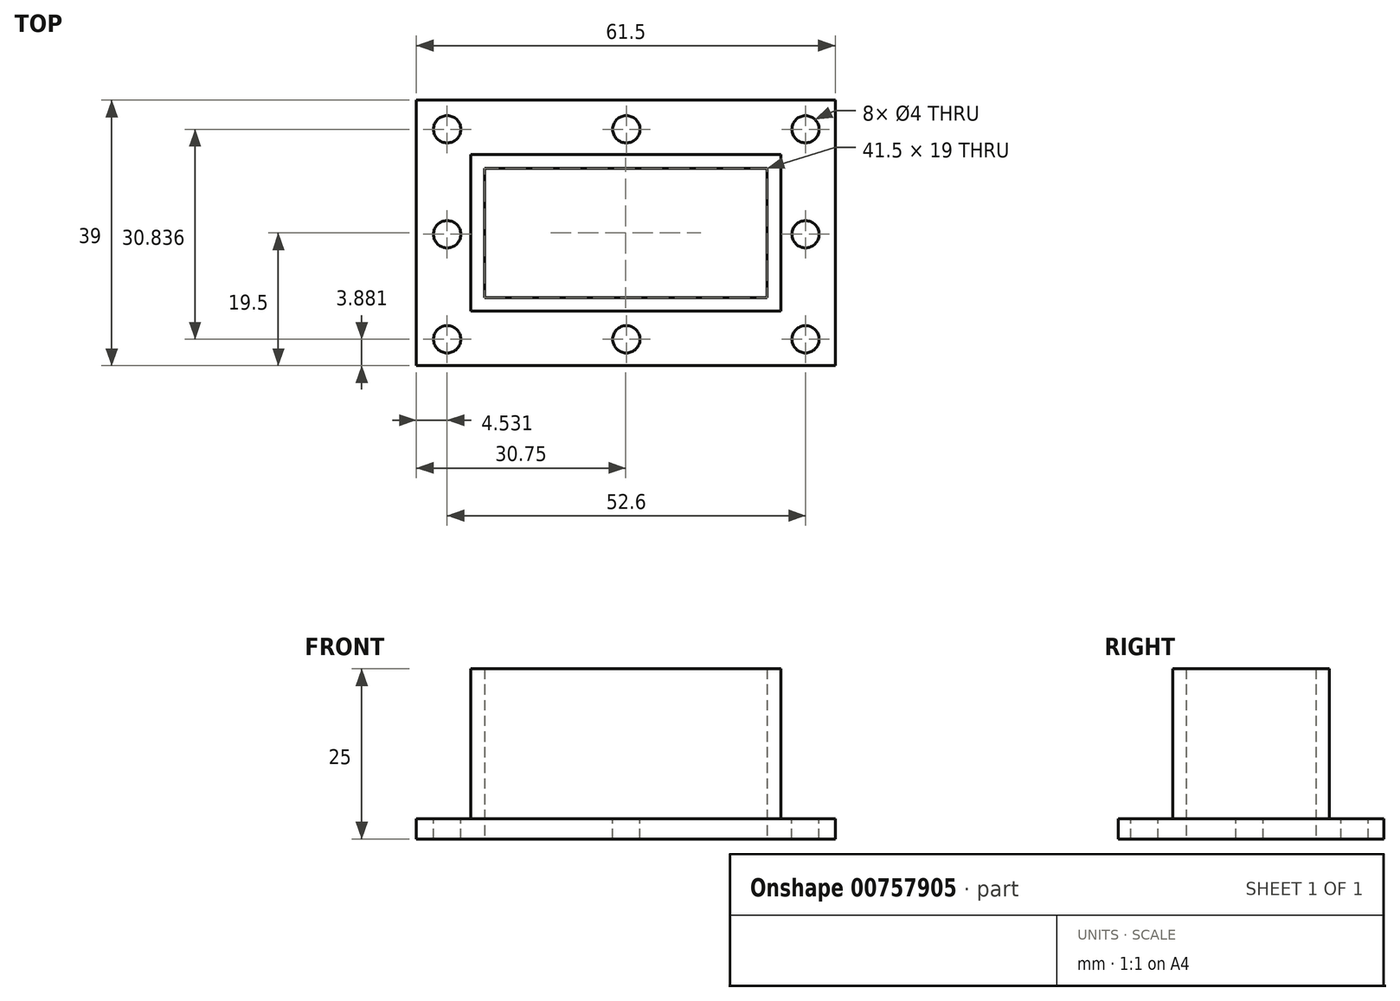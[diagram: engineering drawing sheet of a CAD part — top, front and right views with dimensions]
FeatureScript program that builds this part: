
annotation { "Feature Type Name" : "Feature", "Feature Type Description" : "" }
export const myFeature = defineFeature(function(context is Context, id is Id, definition is map)
    precondition{}
    {
        {
            var Q0;
            Q0=qCreatedBy(makeId("Top.planeOp"),FACE);
            var sketch = newSketch(context, id + "F0", { "sketchPlane" : qUnion([Q0])});
            skLineSegment(sketch, "E0.bottom", {"start": v(0, 0) * mm, "end": v(-41.5, 0) * mm});
            skLineSegment(sketch, "E0.top", {"start": v(0, 19) * mm, "end": v(-41.5, 19) * mm});
            skLineSegment(sketch, "E0.left", {"start": v(0, 0) * mm, "end": v(0, 19) * mm});
            skLineSegment(sketch, "E0.right", {"start": v(-41.5, 0) * mm, "end": v(-41.5, 19) * mm});
            skLineSegment(sketch, "E1.0", {"start": v(2, 21) * mm, "end": v(-43.5, 21) * mm});
            skLineSegment(sketch, "E1.1", {"start": v(2, -2) * mm, "end": v(2, 21) * mm});
            skLineSegment(sketch, "E1.2", {"start": v(2, -2) * mm, "end": v(-43.5, -2) * mm});
            skLineSegment(sketch, "E1.3", {"start": v(-43.5, -2) * mm, "end": v(-43.5, 21) * mm});
            skLineSegment(sketch, "E2.0", {"start": v(10, 29) * mm, "end": v(-51.5, 29) * mm});
            skLineSegment(sketch, "E2.1", {"start": v(10, -10) * mm, "end": v(10, 29) * mm});
            skLineSegment(sketch, "E2.2", {"start": v(10, -10) * mm, "end": v(-51.5, -10) * mm});
            skLineSegment(sketch, "E2.3", {"start": v(-51.5, -10) * mm, "end": v(-51.5, 29) * mm});
            skSolve(sketch);
        }
        {
            var Q0;
            Q0=makeQuery(id+"F0.imprint","IMPRINT",FACE,{"disambiguationData":[TD([[makeQuery(id+"F0.imprint","IMPRINT",EDGE,{"derivedFrom":sQuery(id+"F0.wireOp",EDGE,"E0.bottom")}),1.0]])]});
            extrude(context, id + "F1", {"entities" : qUnion([Q0]), "depth" : 25 * mm, "offsetDistance" : 25 * mm});
        }
        {
            var Q0;
            Q0=makeQuery(id+"F0.imprint","IMPRINT",FACE,{"disambiguationData":[TD([[makeQuery(id+"F0.imprint","IMPRINT",EDGE,{"derivedFrom":sQuery(id+"F0.wireOp",EDGE,"E1.0")}),-1.0]])]});
            extrude(context, id + "F2", {"entities" : qUnion([Q0]), "operationType" : NewBodyOperationType.ADD, "depth" : 3 * mm, "offsetDistance" : 25 * mm});
        }
        {
            var Q0;
            Q0=makeQuery(id+"F2.opExtrude","CAP_FACE",FACE,{"disambiguationData":[OSD([sQuery(id+"F0.wireOp",EDGE,"E1.0"),sQuery(id+"F0.wireOp",EDGE,"E1.1"),sQuery(id+"F0.wireOp",EDGE,"E1.2"),sQuery(id+"F0.wireOp",EDGE,"E1.3"),sQuery(id+"F0.wireOp",EDGE,"E2.0"),sQuery(id+"F0.wireOp",EDGE,"E2.1"),sQuery(id+"F0.wireOp",EDGE,"E2.2"),sQuery(id+"F0.wireOp",EDGE,"E2.3")])],"isStart":false});
            var sketch = newSketch(context, id + "F3", { "sketchPlane" : qUnion([Q0])});
            skCircle(sketch, "E3", {"center": v(-46.97, 24.72) * mm, "radius": 2 * mm});
            skCircle(sketch, "E4.1.0.0", {"center": v(-20.67, 24.72) * mm, "radius": 2 * mm});
            skCircle(sketch, "E4.2.0.0", {"center": v(5.63, 24.72) * mm, "radius": 2 * mm});
            skLineSegment(sketch, "E4.direction1", {"start": v(-46.97, 24.72) * mm, "end": v(-20.67, 24.72) * mm, "construction": true});
            skCircle(sketch, "E5.1.0.0", {"center": v(-46.97, 9.3) * mm, "radius": 2 * mm});
            skCircle(sketch, "E5.1.0.2", {"center": v(5.63, 9.3) * mm, "radius": 2 * mm});
            skLineSegment(sketch, "E5.1.0.3", {"start": v(-46.97, 9.3) * mm, "end": v(-20.67, 9.3) * mm, "construction": true});
            skCircle(sketch, "E5.2.0.0", {"center": v(-46.97, -6.12) * mm, "radius": 2 * mm});
            skCircle(sketch, "E5.2.0.1", {"center": v(-20.67, -6.12) * mm, "radius": 2 * mm});
            skCircle(sketch, "E5.2.0.2", {"center": v(5.63, -6.12) * mm, "radius": 2 * mm});
            skLineSegment(sketch, "E5.2.0.3", {"start": v(-46.97, -6.12) * mm, "end": v(-20.67, -6.12) * mm, "construction": true});
            skLineSegment(sketch, "E5.direction1", {"start": v(-46.97, 24.72) * mm, "end": v(-46.97, 9.3) * mm, "construction": true});
            skSolve(sketch);
        }
        {
            var Q0;
            Q0 = qSketchRegion(id + "F3", true);
            extrude(context, id + "F4", {"entities" : qUnion([Q0]), "operationType" : NewBodyOperationType.REMOVE, "endBound" : BoundingType.THROUGH_ALL, "oppositeDirection" : true, "depth" : 25 * mm, "offsetDistance" : 25 * mm});
        }
    });
